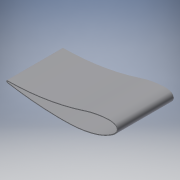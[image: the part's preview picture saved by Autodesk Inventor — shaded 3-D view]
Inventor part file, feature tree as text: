
AUTODESK INVENTOR PART (.ipt)
format: ipt  version: 2018.2 (Build 222227000, 227)  size: 130,048 bytes
history: native  units: mm
features: extrude x1, shell x1, sketch x1, projected_geometry x1
ambient origin geometry x8: Origin, YZ Plane, XZ Plane, XY Plane, X Axis, Y Axis, Z Axis, Center Point
bodies: Body1 (feature_tree)
feature tree (4):
  extrude  "押し出し1"  Depth=186.0mm TaperAngle=0.0deg
  shell  "シェル1"  Thickness=3.0mm
  sketch  "スケッチ1"
  projected_geometry  "投影ループ1"
